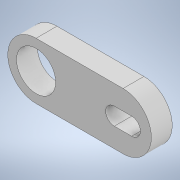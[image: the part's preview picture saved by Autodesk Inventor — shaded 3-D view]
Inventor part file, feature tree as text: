
AUTODESK INVENTOR PART (.ipt)
format: ipt  version: 2020 (Build 240168000, 168)  size: 118,272 bytes
history: native  units: in
note: dims shown in document units (in); Inventor stores cm internally (conversion verified against a paired STEP export)
features: extrude x2, sketch x2
ambient origin geometry x8: Origin, YZ Plane, XZ Plane, XY Plane, X Axis, Y Axis, Z Axis, Center Point
bodies: Solid1 (feature_tree)
feature tree (4):
  extrude  "Extrusion1"  Depth=0.813in
  extrude  "Extrusion2"  Depth=0.25in
  sketch  "Sketch1"  dims[d0=0.813in d1=2.5in]
  sketch  "Sketch2"  dims[d2=0.6in d3=0.0in d4=1.126in d5=0.5in d6=0.25in d7=1.0in d8=0.0in d9=0.0in]
